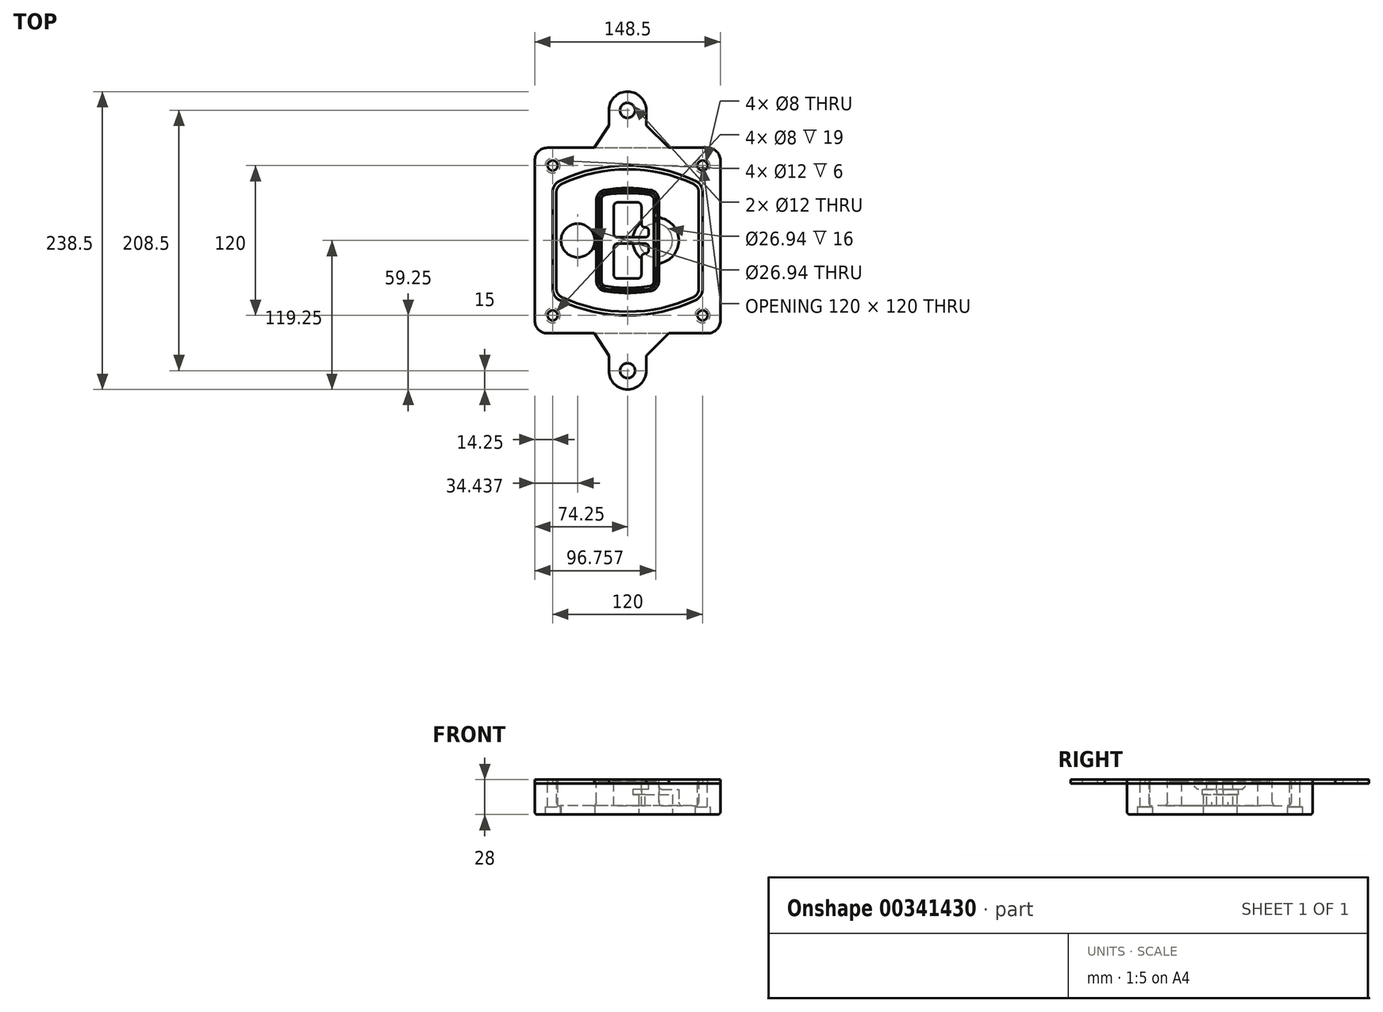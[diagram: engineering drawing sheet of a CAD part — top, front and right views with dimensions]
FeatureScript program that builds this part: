
annotation { "Feature Type Name" : "Feature", "Feature Type Description" : "" }
export const myFeature = defineFeature(function(context is Context, id is Id, definition is map)
    precondition{}
    {
        {
            var Q0;
            Q0=qCreatedBy(makeId("Top.planeOp"),FACE);
            var sketch = newSketch(context, id + "F0", { "sketchPlane" : qUnion([Q0])});
            skPoint(sketch, "E0.rect.middle", {"position": v(0, 0) * mm});
            skLineSegment(sketch, "E1.bottom", {"start": v(-64.25, -74.25) * mm, "end": v(64.25, -74.25) * mm});
            skLineSegment(sketch, "E1.top", {"start": v(-64.25, 74.25) * mm, "end": v(64.25, 74.25) * mm});
            skLineSegment(sketch, "E1.left", {"start": v(-74.25, -64.25) * mm, "end": v(-74.25, 64.25) * mm});
            skLineSegment(sketch, "E1.right", {"start": v(74.25, -64.25) * mm, "end": v(74.25, 64.25) * mm});
            skLineSegment(sketch, "E2", {"start": v(-74.25, 74.25) * mm, "end": v(74.25, -74.25) * mm, "construction": true});
            skLineSegment(sketch, "E3", {"start": v(74.25, 74.25) * mm, "end": v(-74.25, -74.25) * mm, "construction": true});
            skCircle(sketch, "E4", {"center": v(-60, 60) * mm, "radius": 4 * mm});
            skCircle(sketch, "E5", {"center": v(60, 60) * mm, "radius": 4 * mm});
            skCircle(sketch, "E6", {"center": v(60, -60) * mm, "radius": 4 * mm});
            skCircle(sketch, "E7", {"center": v(-60, -60) * mm, "radius": 4 * mm});
            skLineSegment(sketch, "E8", {"start": v(-60, 60) * mm, "end": v(60, 60) * mm, "construction": true});
            skLineSegment(sketch, "E9", {"start": v(60, 60) * mm, "end": v(60, -60) * mm, "construction": true});
            skLineSegment(sketch, "E10", {"start": v(60, -60) * mm, "end": v(-60, -60) * mm, "construction": true});
            skLineSegment(sketch, "E11", {"start": v(-60, -60) * mm, "end": v(-60, 60) * mm, "construction": true});
            skLineSegment(sketch, "E12", {"start": v(-60, 38.83) * mm, "end": v(-60, -38.83) * mm});
            skLineSegment(sketch, "E13", {"start": v(60, 38.83) * mm, "end": v(60, -38.83) * mm});
            skArc(sketch, "E14", {"start": v(54.26, 47.88) * mm, "mid": v(0, 60) * mm, "end": v(-54.26, 47.88) * mm});
            skArc(sketch, "E15", {"start": v(-54.26, -47.88) * mm, "mid": v(0, -60) * mm, "end": v(54.26, -47.88) * mm});
            skLineSegment(sketch, "E16", {"start": v(-60, 0) * mm, "end": v(60, 0) * mm, "construction": true});
            skPoint(sketch, "E17.visualSharp", {"position": v(-60, -45) * mm});
            skArc(sketch, "E17.filletArc", {"start": v(-60, -38.83) * mm, "mid": v(-58.44, -44.2) * mm, "end": v(-54.26, -47.88) * mm});
            skPoint(sketch, "E18.visualSharp", {"position": v(-60, 45) * mm});
            skArc(sketch, "E18.filletArc", {"start": v(-54.26, 47.88) * mm, "mid": v(-58.44, 44.2) * mm, "end": v(-60, 38.83) * mm});
            skPoint(sketch, "E19.visualSharp", {"position": v(60, 45) * mm});
            skArc(sketch, "E19.filletArc", {"start": v(60, 38.83) * mm, "mid": v(58.44, 44.2) * mm, "end": v(54.26, 47.88) * mm});
            skPoint(sketch, "E20.visualSharp", {"position": v(60, -45) * mm});
            skArc(sketch, "E20.filletArc", {"start": v(54.26, -47.88) * mm, "mid": v(58.44, -44.2) * mm, "end": v(60, -38.83) * mm});
            skPoint(sketch, "E21.visualSharp", {"position": v(-74.25, 74.25) * mm});
            skArc(sketch, "E21.filletArc", {"start": v(-64.25, 74.25) * mm, "mid": v(-71.32, 71.32) * mm, "end": v(-74.25, 64.25) * mm});
            skPoint(sketch, "E22.visualSharp", {"position": v(74.25, 74.25) * mm});
            skArc(sketch, "E22.filletArc", {"start": v(74.25, 64.25) * mm, "mid": v(71.32, 71.32) * mm, "end": v(64.25, 74.25) * mm});
            skPoint(sketch, "E23.visualSharp", {"position": v(74.25, -74.25) * mm});
            skArc(sketch, "E23.filletArc", {"start": v(64.25, -74.25) * mm, "mid": v(71.32, -71.32) * mm, "end": v(74.25, -64.25) * mm});
            skPoint(sketch, "E24.visualSharp", {"position": v(-74.25, -74.25) * mm});
            skArc(sketch, "E24.filletArc", {"start": v(-74.25, -64.25) * mm, "mid": v(-71.32, -71.32) * mm, "end": v(-64.25, -74.25) * mm});
            skArc(sketch, "E25.0", {"start": v(57, 38.83) * mm, "mid": v(55.9, 42.58) * mm, "end": v(52.98, 45.17) * mm});
            skLineSegment(sketch, "E25.1", {"start": v(57, 38.83) * mm, "end": v(57, -38.83) * mm});
            skArc(sketch, "E25.2", {"start": v(52.98, -45.17) * mm, "mid": v(55.9, -42.58) * mm, "end": v(57, -38.83) * mm});
            skArc(sketch, "E25.3", {"start": v(-52.98, -45.17) * mm, "mid": v(0, -57) * mm, "end": v(52.98, -45.17) * mm});
            skArc(sketch, "E25.4", {"start": v(-57, -38.83) * mm, "mid": v(-55.9, -42.58) * mm, "end": v(-52.98, -45.17) * mm});
            skArc(sketch, "E25.5", {"start": v(52.98, 45.17) * mm, "mid": v(0, 57) * mm, "end": v(-52.98, 45.17) * mm});
            skLineSegment(sketch, "E25.6", {"start": v(-57, 38.83) * mm, "end": v(-57, -38.83) * mm});
            skArc(sketch, "E25.7", {"start": v(-52.98, 45.17) * mm, "mid": v(-55.9, 42.58) * mm, "end": v(-57, 38.83) * mm});
            skArc(sketch, "E26.0", {"start": v(-55.96, 51.5) * mm, "mid": v(-61.82, 46.33) * mm, "end": v(-64, 38.83) * mm});
            skArc(sketch, "E26.1", {"start": v(55.96, 51.5) * mm, "mid": v(0, 64) * mm, "end": v(-55.96, 51.5) * mm});
            skArc(sketch, "E26.2", {"start": v(64, 38.83) * mm, "mid": v(61.82, 46.33) * mm, "end": v(55.96, 51.5) * mm});
            skLineSegment(sketch, "E26.3", {"start": v(64, 38.83) * mm, "end": v(64, -38.83) * mm});
            skArc(sketch, "E26.4", {"start": v(55.96, -51.5) * mm, "mid": v(61.82, -46.33) * mm, "end": v(64, -38.83) * mm});
            skLineSegment(sketch, "E26.5", {"start": v(-64, 38.83) * mm, "end": v(-64, -38.83) * mm});
            skArc(sketch, "E26.6", {"start": v(-55.96, -51.5) * mm, "mid": v(0, -64) * mm, "end": v(55.96, -51.5) * mm});
            skArc(sketch, "E26.7", {"start": v(-64, -38.83) * mm, "mid": v(-61.82, -46.33) * mm, "end": v(-55.96, -51.5) * mm});
            skSolve(sketch);
        }
        {
            var Q0;
            Q0=makeQuery(id+"F0.imprint","IMPRINT",FACE,{"disambiguationData":[TD([[makeQuery(id+"F0.imprint","IMPRINT",EDGE,{"derivedFrom":sQuery(id+"F0.wireOp",EDGE,"E1.bottom")}),1.0]])]});
            var Q1;
            Q1=makeQuery(id+"F0.imprint","IMPRINT",FACE,{"disambiguationData":[TD([[makeQuery(id+"F0.imprint","IMPRINT",EDGE,{"derivedFrom":sQuery(id+"F0.wireOp",EDGE,"E12")}),1.0]])]});
            var Q2;
            Q2=makeQuery(id+"F0.imprint","IMPRINT",FACE,{"disambiguationData":[TD([[makeQuery(id+"F0.imprint","IMPRINT",EDGE,{"derivedFrom":sQuery(id+"F0.wireOp",EDGE,"E25.0")}),1.0]])]});
            var Q3;
            Q3=makeQuery(id+"F0.imprint","IMPRINT",FACE,{"disambiguationData":[TD([[makeQuery(id+"F0.imprint","IMPRINT",EDGE,{"derivedFrom":sQuery(id+"F0.wireOp",EDGE,"E12")}),-1.0]])]});
            extrude(context, id + "F1", {"entities" : qUnion([Q0, Q1, Q2, Q3]), "oppositeDirection" : true, "depth" : 25 * mm});
        }
        {
            var Q0;
            Q0=makeQuery(id+"F0.imprint","IMPRINT",FACE,{"disambiguationData":[TD([[makeQuery(id+"F0.imprint","IMPRINT",EDGE,{"derivedFrom":sQuery(id+"F0.wireOp",EDGE,"E12")}),1.0]])]});
            extrude(context, id + "F2", {"entities" : qUnion([Q0]), "operationType" : NewBodyOperationType.ADD, "depth" : 3 * mm});
        }
        {
            var Q0;
            Q0=makeQuery(id+"F0.imprint","IMPRINT",FACE,{"disambiguationData":[TD([[makeQuery(id+"F0.imprint","IMPRINT",EDGE,{"derivedFrom":sQuery(id+"F0.wireOp",EDGE,"E25.0")}),1.0]])]});
            extrude(context, id + "F3", {"entities" : qUnion([Q0]), "operationType" : NewBodyOperationType.REMOVE, "oppositeDirection" : true, "depth" : 18 * mm});
        }
        {
            var Q0;
            Q0=makeQuery(id+"F2.opExtrude","CAP_FACE",FACE,{"disambiguationData":[OSD([sQuery(id+"F0.wireOp",EDGE,"E12"),sQuery(id+"F0.wireOp",EDGE,"E13"),sQuery(id+"F0.wireOp",EDGE,"E14"),sQuery(id+"F0.wireOp",EDGE,"E15"),sQuery(id+"F0.wireOp",EDGE,"E17.filletArc"),sQuery(id+"F0.wireOp",EDGE,"E18.filletArc"),sQuery(id+"F0.wireOp",EDGE,"E19.filletArc"),sQuery(id+"F0.wireOp",EDGE,"E20.filletArc"),sQuery(id+"F0.wireOp",EDGE,"E25.0"),sQuery(id+"F0.wireOp",EDGE,"E25.1"),sQuery(id+"F0.wireOp",EDGE,"E25.2"),sQuery(id+"F0.wireOp",EDGE,"E25.3"),sQuery(id+"F0.wireOp",EDGE,"E25.4"),sQuery(id+"F0.wireOp",EDGE,"E25.5"),sQuery(id+"F0.wireOp",EDGE,"E25.6"),sQuery(id+"F0.wireOp",EDGE,"E25.7")])],"isStart":false});
            var sketch = newSketch(context, id + "F4", { "sketchPlane" : qUnion([Q0])});
            skArc(sketch, "E27.0", {"start": v(-18.34, -40.45) * mm, "mid": v(0, -42) * mm, "end": v(18.34, -40.45) * mm});
            skArc(sketch, "E28.0", {"start": v(18.34, 40.45) * mm, "mid": v(0, 42) * mm, "end": v(-18.34, 40.45) * mm});
            skLineSegment(sketch, "E29", {"start": v(-25, 32.57) * mm, "end": v(-25, -32.57) * mm});
            skLineSegment(sketch, "E30", {"start": v(25, 32.57) * mm, "end": v(25, -32.57) * mm});
            skLineSegment(sketch, "E31", {"start": v(-25, 39.1) * mm, "end": v(25, 39.1) * mm, "construction": true});
            skLineSegment(sketch, "E32", {"start": v(-25, -39.1) * mm, "end": v(25, -39.1) * mm, "construction": true});
            skPoint(sketch, "E33.visualSharp", {"position": v(-25, 39.1) * mm});
            skArc(sketch, "E33.filletArc", {"start": v(-18.34, 40.45) * mm, "mid": v(-23.11, 37.73) * mm, "end": v(-25, 32.57) * mm});
            skPoint(sketch, "E34.visualSharp", {"position": v(25, 39.1) * mm});
            skArc(sketch, "E34.filletArc", {"start": v(25, 32.57) * mm, "mid": v(23.11, 37.73) * mm, "end": v(18.34, 40.45) * mm});
            skPoint(sketch, "E35.visualSharp", {"position": v(25, -39.1) * mm});
            skArc(sketch, "E35.filletArc", {"start": v(18.34, -40.45) * mm, "mid": v(23.11, -37.73) * mm, "end": v(25, -32.57) * mm});
            skPoint(sketch, "E36.visualSharp", {"position": v(-25, -39.1) * mm});
            skArc(sketch, "E36.filletArc", {"start": v(-25, -32.57) * mm, "mid": v(-23.11, -37.73) * mm, "end": v(-18.34, -40.45) * mm});
            skArc(sketch, "E37.0", {"start": v(52.98, 45.17) * mm, "mid": v(0, 57) * mm, "end": v(-52.98, 45.17) * mm});
            skArc(sketch, "E37.1", {"start": v(-52.98, 45.17) * mm, "mid": v(-55.9, 42.58) * mm, "end": v(-57, 38.83) * mm});
            skLineSegment(sketch, "E37.2", {"start": v(-57, 38.83) * mm, "end": v(-57, -38.83) * mm});
            skArc(sketch, "E37.3", {"start": v(-57, -38.83) * mm, "mid": v(-55.9, -42.58) * mm, "end": v(-52.98, -45.17) * mm});
            skArc(sketch, "E37.4", {"start": v(-52.98, -45.17) * mm, "mid": v(0, -57) * mm, "end": v(52.98, -45.17) * mm});
            skArc(sketch, "E37.5", {"start": v(52.98, -45.17) * mm, "mid": v(55.9, -42.58) * mm, "end": v(57, -38.83) * mm});
            skLineSegment(sketch, "E37.6", {"start": v(57, 38.83) * mm, "end": v(57, -38.83) * mm});
            skArc(sketch, "E37.7", {"start": v(57, 38.83) * mm, "mid": v(55.9, 42.58) * mm, "end": v(52.98, 45.17) * mm});
            skLineSegment(sketch, "E38.0", {"start": v(23, 32.57) * mm, "end": v(23, -32.57) * mm});
            skArc(sketch, "E38.1", {"start": v(18, -38.48) * mm, "mid": v(21.58, -36.44) * mm, "end": v(23, -32.57) * mm});
            skArc(sketch, "E38.2", {"start": v(-18, -38.48) * mm, "mid": v(0, -40) * mm, "end": v(18, -38.48) * mm});
            skArc(sketch, "E38.3", {"start": v(-23, -32.57) * mm, "mid": v(-21.58, -36.44) * mm, "end": v(-18, -38.48) * mm});
            skLineSegment(sketch, "E38.4", {"start": v(-23, 32.57) * mm, "end": v(-23, -32.57) * mm});
            skArc(sketch, "E38.5", {"start": v(23, 32.57) * mm, "mid": v(21.58, 36.44) * mm, "end": v(18, 38.48) * mm});
            skArc(sketch, "E38.6", {"start": v(-18, 38.48) * mm, "mid": v(-21.58, 36.44) * mm, "end": v(-23, 32.57) * mm});
            skArc(sketch, "E38.7", {"start": v(18, 38.48) * mm, "mid": v(0, 40) * mm, "end": v(-18, 38.48) * mm});
            skArc(sketch, "E39.0", {"start": v(21, 32.57) * mm, "mid": v(20.06, 35.15) * mm, "end": v(17.67, 36.5) * mm});
            skLineSegment(sketch, "E39.1", {"start": v(21, 32.57) * mm, "end": v(21, -32.57) * mm});
            skArc(sketch, "E39.2", {"start": v(17.67, -36.5) * mm, "mid": v(20.06, -35.15) * mm, "end": v(21, -32.57) * mm});
            skArc(sketch, "E39.3", {"start": v(-17.67, -36.5) * mm, "mid": v(0, -38) * mm, "end": v(17.67, -36.5) * mm});
            skArc(sketch, "E39.4", {"start": v(-21, -32.57) * mm, "mid": v(-20.06, -35.15) * mm, "end": v(-17.67, -36.5) * mm});
            skArc(sketch, "E39.5", {"start": v(17.67, 36.5) * mm, "mid": v(0, 38) * mm, "end": v(-17.67, 36.5) * mm});
            skLineSegment(sketch, "E39.6", {"start": v(-21, 32.57) * mm, "end": v(-21, -32.57) * mm});
            skArc(sketch, "E39.7", {"start": v(-17.67, 36.5) * mm, "mid": v(-20.06, 35.15) * mm, "end": v(-21, 32.57) * mm});
            skLineSegment(sketch, "E40", {"start": v(-25, 0) * mm, "end": v(25, 0) * mm, "construction": true});
            skLineSegment(sketch, "E41", {"start": v(-11, 5.5) * mm, "end": v(-11, 27.5) * mm});
            skLineSegment(sketch, "E42", {"start": v(-8, 30.5) * mm, "end": v(8, 30.5) * mm});
            skLineSegment(sketch, "E43", {"start": v(11, 27.5) * mm, "end": v(11, 13.5) * mm});
            skLineSegment(sketch, "E44", {"start": v(14, 10.5) * mm, "end": v(14, 10.5) * mm});
            skLineSegment(sketch, "E45", {"start": v(17, 7.5) * mm, "end": v(17, 5.5) * mm});
            skLineSegment(sketch, "E46", {"start": v(14, 2.5) * mm, "end": v(-8, 2.5) * mm});
            skPoint(sketch, "E47.visualSharp", {"position": v(-11, 30.5) * mm});
            skArc(sketch, "E47.filletArc", {"start": v(-8, 30.5) * mm, "mid": v(-10.12, 29.62) * mm, "end": v(-11, 27.5) * mm});
            skPoint(sketch, "E48.visualSharp", {"position": v(11, 30.5) * mm});
            skArc(sketch, "E48.filletArc", {"start": v(11, 27.5) * mm, "mid": v(10.12, 29.62) * mm, "end": v(8, 30.5) * mm});
            skPoint(sketch, "E49.visualSharp", {"position": v(11, 10.5) * mm});
            skArc(sketch, "E49.filletArc", {"start": v(11, 13.5) * mm, "mid": v(11.88, 11.38) * mm, "end": v(14, 10.5) * mm});
            skPoint(sketch, "E50.visualSharp", {"position": v(17, 10.5) * mm});
            skArc(sketch, "E50.filletArc", {"start": v(17, 7.5) * mm, "mid": v(16.12, 9.62) * mm, "end": v(14, 10.5) * mm});
            skPoint(sketch, "E51.visualSharp", {"position": v(17, 2.5) * mm});
            skArc(sketch, "E51.filletArc", {"start": v(14, 2.5) * mm, "mid": v(16.12, 3.38) * mm, "end": v(17, 5.5) * mm});
            skPoint(sketch, "E52.visualSharp", {"position": v(-11, 2.5) * mm});
            skArc(sketch, "E52.filletArc", {"start": v(-11, 5.5) * mm, "mid": v(-10.12, 3.38) * mm, "end": v(-8, 2.5) * mm});
            skLineSegment(sketch, "E53.0.MirrorCS", {"start": v(14, -2.5) * mm, "end": v(-8, -2.5) * mm});
            skArc(sketch, "E54.0.MirrorCS", {"start": v(-11, -5.5) * mm, "mid": v(-10.12, -3.38) * mm, "end": v(-8, -2.5) * mm});
            skLineSegment(sketch, "E55.0.MirrorCS", {"start": v(-11, -5.5) * mm, "end": v(-11, -27.5) * mm});
            skArc(sketch, "E56.0.MirrorCS", {"start": v(-8, -30.5) * mm, "mid": v(-10.12, -29.62) * mm, "end": v(-11, -27.5) * mm});
            skLineSegment(sketch, "E57.0.MirrorCS", {"start": v(-8, -30.5) * mm, "end": v(8, -30.5) * mm});
            skArc(sketch, "E58.0.MirrorCS", {"start": v(11, -27.5) * mm, "mid": v(10.12, -29.62) * mm, "end": v(8, -30.5) * mm});
            skLineSegment(sketch, "E59.0.MirrorCS", {"start": v(11, -27.5) * mm, "end": v(11, -13.5) * mm});
            skArc(sketch, "E60.0.MirrorCS", {"start": v(11, -13.5) * mm, "mid": v(11.88, -11.38) * mm, "end": v(14, -10.5) * mm});
            skArc(sketch, "E61.0.MirrorCS", {"start": v(17, -7.5) * mm, "mid": v(16.12, -9.62) * mm, "end": v(14, -10.5) * mm});
            skLineSegment(sketch, "E62.0.MirrorCS", {"start": v(17, -7.5) * mm, "end": v(17, -5.5) * mm});
            skArc(sketch, "E63.0.MirrorCS", {"start": v(14, -2.5) * mm, "mid": v(16.12, -3.38) * mm, "end": v(17, -5.5) * mm});
            skSolve(sketch);
        }
        {
            var Q0;
            Q0=makeQuery(id+"F4.imprint","IMPRINT",FACE,{"disambiguationData":[TD([[makeQuery(id+"F4.imprint","IMPRINT",EDGE,{"derivedFrom":sQuery(id+"F4.wireOp",EDGE,"E27.0")}),1.0]])]});
            var Q1;
            Q1=makeQuery(id+"F4.imprint","IMPRINT",FACE,{"disambiguationData":[TD([[makeQuery(id+"F4.imprint","IMPRINT",EDGE,{"derivedFrom":sQuery(id+"F4.wireOp",EDGE,"E38.0")}),-1.0]])]});
            var Q2;
            Q2=makeQuery(id+"F4.imprint","IMPRINT",FACE,{"disambiguationData":[TD([[makeQuery(id+"F4.imprint","IMPRINT",EDGE,{"derivedFrom":sQuery(id+"F4.wireOp",EDGE,"E39.0")}),1.0]])]});
            extrude(context, id + "F5", {"entities" : qUnion([Q0, Q1, Q2]), "operationType" : NewBodyOperationType.ADD, "endBound" : BoundingType.UP_TO_NEXT, "oppositeDirection" : true, "depth" : 25 * mm});
        }
        {
            var Q0;
            Q0=makeQuery(id+"F4.imprint","IMPRINT",FACE,{"disambiguationData":[TD([[makeQuery(id+"F4.imprint","IMPRINT",EDGE,{"derivedFrom":sQuery(id+"F4.wireOp",EDGE,"E38.0")}),-1.0]])]});
            extrude(context, id + "F6", {"entities" : qUnion([Q0]), "operationType" : NewBodyOperationType.REMOVE, "oppositeDirection" : true, "depth" : 2 * mm});
        }
        {
            var Q0;
            Q0=makeQuery(id+"F1.opExtrude","CAP_FACE",FACE,{"disambiguationData":[OSD([sQuery(id+"F0.wireOp",EDGE,"E1.bottom"),sQuery(id+"F0.wireOp",EDGE,"E1.top"),sQuery(id+"F0.wireOp",EDGE,"E1.left"),sQuery(id+"F0.wireOp",EDGE,"E1.right"),sQuery(id+"F0.wireOp",EDGE,"E4"),sQuery(id+"F0.wireOp",EDGE,"E5"),sQuery(id+"F0.wireOp",EDGE,"E6"),sQuery(id+"F0.wireOp",EDGE,"E7"),sQuery(id+"F0.wireOp",EDGE,"E21.filletArc"),sQuery(id+"F0.wireOp",EDGE,"E22.filletArc"),sQuery(id+"F0.wireOp",EDGE,"E23.filletArc"),sQuery(id+"F0.wireOp",EDGE,"E24.filletArc")])],"isStart":false});
            var sketch = newSketch(context, id + "F7", { "sketchPlane" : qUnion([Q0])});
            skCircle(sketch, "E64", {"center": v(22.5, 0) * mm, "radius": 13.47 * mm});
            skCircle(sketch, "E65", {"center": v(-39.81, 0) * mm, "radius": 13.47 * mm});
            skLineSegment(sketch, "E66", {"start": v(74.25, 0) * mm, "end": v(-74.25, 0) * mm});
            skCircle(sketch, "E67", {"center": v(22.5, 0) * mm, "radius": 18.47 * mm});
            skCircle(sketch, "E68", {"center": v(60, -60) * mm, "radius": 6 * mm});
            skCircle(sketch, "E69", {"center": v(-60, -60) * mm, "radius": 6 * mm});
            skCircle(sketch, "E70", {"center": v(-60, 60) * mm, "radius": 6 * mm});
            skCircle(sketch, "E71", {"center": v(60, 60) * mm, "radius": 6 * mm});
            skSolve(sketch);
        }
        {
            var Q0;
            {var subQ1=sQuery(id+"F7.wireOp",EDGE,"E66");var subQ4=sQuery(id+"F7.wireOp",EDGE,"E64");var subQ6=makeQuery(id+"F7.imprint","INTERSECT",VERTEX,{"disambiguationData":[OD(0.0)],"derivedFrom":[subQ4,subQ1]});Q0=makeQuery(id+"F7.imprint","IMPRINT",FACE,{"disambiguationData":[TD([[makeQuery(id+"F7.imprint","IMPRINT",EDGE,{"disambiguationData":[TD([[subQ6,-1.0]])],"derivedFrom":subQ4}),-1.0]])]});}
            var Q1;
            {var subQ0=sQuery(id+"F7.wireOp",EDGE,"E66");var subQ1=sQuery(id+"F7.wireOp",EDGE,"E64");var subQ3=makeQuery(id+"F7.imprint","INTERSECT",VERTEX,{"disambiguationData":[OD(0.0)],"derivedFrom":[subQ1,subQ0]});Q1=makeQuery(id+"F7.imprint","IMPRINT",FACE,{"disambiguationData":[TD([[makeQuery(id+"F7.imprint","IMPRINT",EDGE,{"disambiguationData":[TD([[subQ3,-1.0]])],"derivedFrom":subQ1}),1.0]])]});}
            var Q2;
            {var subQ0=sQuery(id+"F7.wireOp",EDGE,"E66");var subQ1=sQuery(id+"F7.wireOp",EDGE,"E64");var subQ3=makeQuery(id+"F7.imprint","INTERSECT",VERTEX,{"disambiguationData":[OD(0.0)],"derivedFrom":[subQ1,subQ0]});Q2=makeQuery(id+"F7.imprint","IMPRINT",FACE,{"disambiguationData":[TD([[makeQuery(id+"F7.imprint","IMPRINT",EDGE,{"disambiguationData":[TD([[subQ3,1.0]])],"derivedFrom":subQ1}),1.0]])]});}
            var Q3;
            {var subQ1=sQuery(id+"F7.wireOp",EDGE,"E66");var subQ4=sQuery(id+"F7.wireOp",EDGE,"E64");var subQ6=makeQuery(id+"F7.imprint","INTERSECT",VERTEX,{"disambiguationData":[OD(0.0)],"derivedFrom":[subQ4,subQ1]});Q3=makeQuery(id+"F7.imprint","IMPRINT",FACE,{"disambiguationData":[TD([[makeQuery(id+"F7.imprint","IMPRINT",EDGE,{"disambiguationData":[TD([[subQ6,1.0]])],"derivedFrom":subQ4}),-1.0]])]});}
            extrude(context, id + "F8", {"entities" : qUnion([Q0, Q1, Q2, Q3]), "operationType" : NewBodyOperationType.ADD, "oppositeDirection" : true, "depth" : 20 * mm});
        }
        {
            var Q0;
            {var subQ0=sQuery(id+"F7.wireOp",EDGE,"E66");var subQ1=sQuery(id+"F7.wireOp",EDGE,"E64");var subQ3=makeQuery(id+"F7.imprint","INTERSECT",VERTEX,{"disambiguationData":[OD(0.0)],"derivedFrom":[subQ1,subQ0]});Q0=makeQuery(id+"F7.imprint","IMPRINT",FACE,{"disambiguationData":[TD([[makeQuery(id+"F7.imprint","IMPRINT",EDGE,{"disambiguationData":[TD([[subQ3,-1.0]])],"derivedFrom":subQ1}),1.0]])]});}
            var Q1;
            {var subQ0=sQuery(id+"F7.wireOp",EDGE,"E66");var subQ1=sQuery(id+"F7.wireOp",EDGE,"E64");var subQ3=makeQuery(id+"F7.imprint","INTERSECT",VERTEX,{"disambiguationData":[OD(0.0)],"derivedFrom":[subQ1,subQ0]});Q1=makeQuery(id+"F7.imprint","IMPRINT",FACE,{"disambiguationData":[TD([[makeQuery(id+"F7.imprint","IMPRINT",EDGE,{"disambiguationData":[TD([[subQ3,1.0]])],"derivedFrom":subQ1}),1.0]])]});}
            extrude(context, id + "F9", {"entities" : qUnion([Q0, Q1]), "operationType" : NewBodyOperationType.REMOVE, "oppositeDirection" : true, "depth" : 16 * mm});
        }
        {
            var Q0;
            {var subQ0=sQuery(id+"F7.wireOp",EDGE,"E66");var subQ1=sQuery(id+"F7.wireOp",EDGE,"E65");var subQ3=makeQuery(id+"F7.imprint","INTERSECT",VERTEX,{"disambiguationData":[OD(0.0)],"derivedFrom":[subQ1,subQ0]});Q0=makeQuery(id+"F7.imprint","IMPRINT",FACE,{"disambiguationData":[TD([[makeQuery(id+"F7.imprint","IMPRINT",EDGE,{"disambiguationData":[TD([[subQ3,-1.0]])],"derivedFrom":subQ1}),1.0]])]});}
            var Q1;
            {var subQ0=sQuery(id+"F7.wireOp",EDGE,"E66");var subQ1=sQuery(id+"F7.wireOp",EDGE,"E65");var subQ3=makeQuery(id+"F7.imprint","INTERSECT",VERTEX,{"disambiguationData":[OD(0.0)],"derivedFrom":[subQ1,subQ0]});Q1=makeQuery(id+"F7.imprint","IMPRINT",FACE,{"disambiguationData":[TD([[makeQuery(id+"F7.imprint","IMPRINT",EDGE,{"disambiguationData":[TD([[subQ3,1.0]])],"derivedFrom":subQ1}),1.0]])]});}
            extrude(context, id + "F10", {"entities" : qUnion([Q0, Q1]), "operationType" : NewBodyOperationType.REMOVE, "oppositeDirection" : true, "depth" : 25 * mm});
        }
        {
            var Q0;
            Q0=makeQuery(id+"F7.imprint","IMPRINT",FACE,{"disambiguationData":[TD([[makeQuery(id+"F7.imprint","IMPRINT",EDGE,{"derivedFrom":sQuery(id+"F7.wireOp",EDGE,"E68")}),1.0]])]});
            var Q1;
            Q1=makeQuery(id+"F7.imprint","IMPRINT",FACE,{"disambiguationData":[TD([[makeQuery(id+"F7.imprint","IMPRINT",EDGE,{"derivedFrom":makeQuery(id+"F1.opExtrude","CAP_EDGE",EDGE,{"disambiguationData":[OSD([sQuery(id+"F0.wireOp",EDGE,"E5")])],"isStart":false})}),-1.0]])]});
            var Q2;
            Q2=makeQuery(id+"F7.imprint","IMPRINT",FACE,{"disambiguationData":[TD([[makeQuery(id+"F7.imprint","IMPRINT",EDGE,{"derivedFrom":sQuery(id+"F7.wireOp",EDGE,"E69")}),1.0]])]});
            var Q3;
            Q3=makeQuery(id+"F7.imprint","IMPRINT",FACE,{"disambiguationData":[TD([[makeQuery(id+"F7.imprint","IMPRINT",EDGE,{"derivedFrom":makeQuery(id+"F1.opExtrude","CAP_EDGE",EDGE,{"disambiguationData":[OSD([sQuery(id+"F0.wireOp",EDGE,"E4")])],"isStart":false})}),-1.0]])]});
            var Q4;
            Q4=makeQuery(id+"F7.imprint","IMPRINT",FACE,{"disambiguationData":[TD([[makeQuery(id+"F7.imprint","IMPRINT",EDGE,{"derivedFrom":sQuery(id+"F7.wireOp",EDGE,"E70")}),1.0]])]});
            var Q5;
            Q5=makeQuery(id+"F7.imprint","IMPRINT",FACE,{"disambiguationData":[TD([[makeQuery(id+"F7.imprint","IMPRINT",EDGE,{"derivedFrom":makeQuery(id+"F1.opExtrude","CAP_EDGE",EDGE,{"disambiguationData":[OSD([sQuery(id+"F0.wireOp",EDGE,"E7")])],"isStart":false})}),-1.0]])]});
            var Q6;
            Q6=makeQuery(id+"F7.imprint","IMPRINT",FACE,{"disambiguationData":[TD([[makeQuery(id+"F7.imprint","IMPRINT",EDGE,{"derivedFrom":sQuery(id+"F7.wireOp",EDGE,"E71")}),1.0]])]});
            var Q7;
            Q7=makeQuery(id+"F7.imprint","IMPRINT",FACE,{"disambiguationData":[TD([[makeQuery(id+"F7.imprint","IMPRINT",EDGE,{"derivedFrom":makeQuery(id+"F1.opExtrude","CAP_EDGE",EDGE,{"disambiguationData":[OSD([sQuery(id+"F0.wireOp",EDGE,"E6")])],"isStart":false})}),-1.0]])]});
            extrude(context, id + "F11", {"entities" : qUnion([Q0, Q1, Q2, Q3, Q4, Q5, Q6, Q7]), "operationType" : NewBodyOperationType.REMOVE, "oppositeDirection" : true, "depth" : 6 * mm});
        }
        {
            var Q0;
            Q0=makeQuery(id+"F9.boolean.opBoolean","COPY",FACE,{"derivedFrom":makeQuery(id+"F9.opExtrude","CAP_FACE",FACE,{"disambiguationData":[OSD([sQuery(id+"F7.wireOp",EDGE,"E64")])],"isStart":false})});
            var sketch = newSketch(context, id + "F12", { "sketchPlane" : qUnion([Q0])});
            skArc(sketch, "E72.0", {"start": v(11, 14.45) * mm, "mid": v(6.45, 9.13) * mm, "end": v(4.2, 2.5) * mm});
            skArc(sketch, "E72.1", {"start": v(4.2, -2.5) * mm, "mid": v(6.45, -9.13) * mm, "end": v(11, -14.45) * mm});
            skLineSegment(sketch, "E73", {"start": v(4.2, -2.5) * mm, "end": v(14, -2.5) * mm});
            skLineSegment(sketch, "E74.0", {"start": v(14, 2.5) * mm, "end": v(4.2, 2.5) * mm});
            skArc(sketch, "E74.1", {"start": v(14, 2.5) * mm, "mid": v(16.12, 3.38) * mm, "end": v(17, 5.5) * mm});
            skLineSegment(sketch, "E74.2", {"start": v(17, 7.5) * mm, "end": v(17, 5.5) * mm});
            skArc(sketch, "E74.3", {"start": v(17, 7.5) * mm, "mid": v(16.12, 9.62) * mm, "end": v(14, 10.5) * mm});
            skArc(sketch, "E74.4", {"start": v(11, 13.5) * mm, "mid": v(11.88, 11.38) * mm, "end": v(14, 10.5) * mm});
            skLineSegment(sketch, "E74.5", {"start": v(11, 14.45) * mm, "end": v(11, 13.5) * mm});
            skLineSegment(sketch, "E74.7", {"start": v(14, -2.5) * mm, "end": v(4.2, -2.5) * mm});
            skArc(sketch, "E74.8", {"start": v(14, -2.5) * mm, "mid": v(16.12, -3.38) * mm, "end": v(17, -5.5) * mm});
            skLineSegment(sketch, "E74.9", {"start": v(17, -7.5) * mm, "end": v(17, -5.5) * mm});
            skArc(sketch, "E74.10", {"start": v(17, -7.5) * mm, "mid": v(16.12, -9.62) * mm, "end": v(14, -10.5) * mm});
            skArc(sketch, "E74.11", {"start": v(11, -13.5) * mm, "mid": v(11.88, -11.38) * mm, "end": v(14, -10.5) * mm});
            skLineSegment(sketch, "E74.12", {"start": v(11, -14.45) * mm, "end": v(11, -13.5) * mm});
            skPoint(sketch, "E75.orphan", {"position": v(11, -27.5) * mm});
            skPoint(sketch, "E76.orphan", {"position": v(-8, -2.5) * mm});
            skPoint(sketch, "E77.orphan", {"position": v(-8, 2.5) * mm});
            skPoint(sketch, "E78.orphan", {"position": v(11, 27.5) * mm});
            skSolve(sketch);
        }
        {
            var Q0;
            {var subQ7=sQuery(id+"F12.wireOp",EDGE,"E72.0");var subQ14=sQuery(id+"F12.wireOp",EDGE,"E72.1");var subQ16=sQuery(id+"F12.wireOp",EDGE,"E74.1");var subQ18=sQuery(id+"F12.wireOp",EDGE,"E74.8");Q0=qUnion([makeQuery(id+"F12.imprint","IMPRINT",FACE,{"disambiguationData":[TD([[makeQuery(id+"F12.imprint","IMPRINT",EDGE,{"derivedFrom":subQ7}),1.0]])]}),makeQuery(id+"F12.imprint","IMPRINT",FACE,{"disambiguationData":[TD([[makeQuery(id+"F12.imprint","IMPRINT",EDGE,{"derivedFrom":subQ14}),1.0]])]}),makeQuery(id+"F12.imprint","IMPRINT",FACE,{"disambiguationData":[TD([[makeQuery(id+"F12.imprint","IMPRINT",EDGE,{"derivedFrom":subQ16}),1.0]])]}),makeQuery(id+"F12.imprint","IMPRINT",FACE,{"disambiguationData":[TD([[makeQuery(id+"F12.imprint","IMPRINT",EDGE,{"derivedFrom":subQ18}),-1.0]])]})]);}
            var Q1;
            Q1=makeQuery(id+"F5.boolean.opBoolean","SPLIT",FACE,{"disambiguationData":[TD([makeQuery(id+"F5.opExtrude","SWEPT_FACE",FACE,{"disambiguationData":[OSD([sQuery(id+"F4.wireOp",EDGE,"E41")])]})])],"derivedFrom":makeQuery(id+"F3.boolean.opBoolean","COPY",FACE,{"derivedFrom":makeQuery(id+"F3.opExtrude","CAP_FACE",FACE,{"disambiguationData":[OSD([sQuery(id+"F0.wireOp",EDGE,"E25.0"),sQuery(id+"F0.wireOp",EDGE,"E25.1"),sQuery(id+"F0.wireOp",EDGE,"E25.2"),sQuery(id+"F0.wireOp",EDGE,"E25.3"),sQuery(id+"F0.wireOp",EDGE,"E25.4"),sQuery(id+"F0.wireOp",EDGE,"E25.5"),sQuery(id+"F0.wireOp",EDGE,"E25.6"),sQuery(id+"F0.wireOp",EDGE,"E25.7")])],"isStart":false})})});
            extrude(context, id + "F13", {"entities" : qUnion([Q0]), "operationType" : NewBodyOperationType.REMOVE, "endBound" : BoundingType.UP_TO_SURFACE, "endBoundEntityFace" : qUnion([Q1]), "depth" : 25 * mm});
        }
        {
            var Q0;
            Q0=makeQuery(id+"F3.boolean.opBoolean","COPY",EDGE,{"derivedFrom":makeQuery(id+"F3.opExtrude","CAP_EDGE",EDGE,{"disambiguationData":[OSD([sQuery(id+"F0.wireOp",EDGE,"E25.6")])],"isStart":false})});
            var Q1;
            Q1=makeQuery(id+"F8.boolean.opBoolean","INTERSECT",EDGE,{"derivedFrom":[makeQuery(id+"F5.opExtrude","SWEPT_FACE",FACE,{"disambiguationData":[OSD([sQuery(id+"F4.wireOp",EDGE,"E30")])]}),makeQuery(id+"F8.opExtrude","CAP_FACE",FACE,{"disambiguationData":[OSD([sQuery(id+"F7.wireOp",EDGE,"E67")])],"isStart":false})]});
            var Q2;
            Q2=makeQuery(id+"F8.boolean.opBoolean","INTERSECT",EDGE,{"disambiguationData":[OD(1.0)],"derivedFrom":[makeQuery(id+"F5.opExtrude","SWEPT_FACE",FACE,{"disambiguationData":[OSD([sQuery(id+"F4.wireOp",EDGE,"E30")])]}),makeQuery(id+"F8.opExtrude","SWEPT_FACE",FACE,{"disambiguationData":[OSD([sQuery(id+"F7.wireOp",EDGE,"E67")])]})]});
            var Q3;
            {var subQ0=sQuery(id+"F4.wireOp",EDGE,"E30");Q3=makeQuery(id+"F8.boolean.opBoolean","SPLIT",EDGE,{"disambiguationData":[TD([makeQuery(id+"F5.opExtrude","SWEPT_FACE",FACE,{"disambiguationData":[OSD([sQuery(id+"F4.wireOp",EDGE,"E35.filletArc")])]})])],"derivedFrom":makeQuery(id+"F5.opExtrude","CAP_EDGE",EDGE,{"disambiguationData":[OSD([subQ0])],"isStart":false})});}
            var Q4;
            {var subQ0=sQuery(id+"F0.wireOp",EDGE,"E25.7");var subQ1=sQuery(id+"F0.wireOp",EDGE,"E25.1");var subQ2=sQuery(id+"F0.wireOp",EDGE,"E25.6");var subQ3=sQuery(id+"F0.wireOp",EDGE,"E25.5");var subQ4=sQuery(id+"F0.wireOp",EDGE,"E25.4");var subQ5=sQuery(id+"F0.wireOp",EDGE,"E25.0");var subQ6=sQuery(id+"F0.wireOp",EDGE,"E25.2");var subQ7=sQuery(id+"F0.wireOp",EDGE,"E25.3");Q4=makeQuery(id+"F8.boolean.opBoolean","INTERSECT",EDGE,{"derivedFrom":[makeQuery(id+"F5.boolean.opBoolean","SPLIT",FACE,{"disambiguationData":[TD([makeQuery(id+"F2.opExtrude","SWEPT_FACE",FACE,{"disambiguationData":[OSD([subQ5])]})])],"derivedFrom":makeQuery(id+"F3.boolean.opBoolean","COPY",FACE,{"derivedFrom":makeQuery(id+"F3.opExtrude","CAP_FACE",FACE,{"disambiguationData":[OSD([subQ5,subQ1,subQ6,subQ7,subQ4,subQ3,subQ2,subQ0])],"isStart":false})})}),makeQuery(id+"F8.opExtrude","SWEPT_FACE",FACE,{"disambiguationData":[OSD([sQuery(id+"F7.wireOp",EDGE,"E67")])]})]});}
            var Q5;
            Q5=makeQuery(id+"F8.boolean.opBoolean","INTERSECT",EDGE,{"disambiguationData":[OD(0.0)],"derivedFrom":[makeQuery(id+"F5.opExtrude","SWEPT_FACE",FACE,{"disambiguationData":[OSD([sQuery(id+"F4.wireOp",EDGE,"E30")])]}),makeQuery(id+"F8.opExtrude","SWEPT_FACE",FACE,{"disambiguationData":[OSD([sQuery(id+"F7.wireOp",EDGE,"E67")])]})]});
            fillet(context, id + "F14", {"entities" : qUnion([Q0, Q1, Q2, Q3, Q4, Q5]), "radius" : 3 * mm, "tangentPropagation" : true, "allowEdgeOverflow" : false});
        }
        {
            var Q0;
            Q0=makeQuery(id+"F1.opExtrude","CAP_EDGE",EDGE,{"disambiguationData":[OSD([sQuery(id+"F0.wireOp",EDGE,"E1.bottom")])],"isStart":false});
            fillet(context, id + "F15", {"entities" : qUnion([Q0]), "radius" : 2 * mm, "tangentPropagation" : true, "allowEdgeOverflow" : false});
        }
        {
            var Q0;
            {var subQ0=sQuery(id+"F0.wireOp",EDGE,"E21.filletArc");var subQ1=sQuery(id+"F0.wireOp",EDGE,"E7");var subQ2=sQuery(id+"F0.wireOp",EDGE,"E6");var subQ3=sQuery(id+"F0.wireOp",EDGE,"E5");var subQ4=sQuery(id+"F0.wireOp",EDGE,"E4");var subQ5=sQuery(id+"F0.wireOp",EDGE,"E22.filletArc");var subQ6=sQuery(id+"F0.wireOp",EDGE,"E1.bottom");var subQ7=sQuery(id+"F0.wireOp",EDGE,"E1.right");var subQ8=sQuery(id+"F0.wireOp",EDGE,"E1.top");var subQ9=sQuery(id+"F0.wireOp",EDGE,"E1.left");var subQ10=sQuery(id+"F0.wireOp",EDGE,"E23.filletArc");var subQ11=sQuery(id+"F0.wireOp",EDGE,"E24.filletArc");Q0=makeQuery(id+"F2.boolean.opBoolean","SPLIT",FACE,{"disambiguationData":[TD([makeQuery(id+"F1.opExtrude","SWEPT_FACE",FACE,{"disambiguationData":[OSD([subQ6])]})])],"derivedFrom":makeQuery(id+"F1.opExtrude","CAP_FACE",FACE,{"disambiguationData":[OSD([subQ6,subQ8,subQ9,subQ7,subQ4,subQ3,subQ2,subQ1,subQ0,subQ5,subQ10,subQ11])],"isStart":true})});}
            var sketch = newSketch(context, id + "F16", { "sketchPlane" : qUnion([Q0])});
            skLineSegment(sketch, "E79", {"start": v(0, 74.25) * mm, "end": v(0, 104.25) * mm, "construction": true});
            skCircle(sketch, "E80", {"center": v(0, 104.25) * mm, "radius": 6 * mm});
            skLineSegment(sketch, "E81", {"start": v(-15, 104.25) * mm, "end": v(-15, 92.25) * mm});
            skLineSegment(sketch, "E82", {"start": v(-15, 92.25) * mm, "end": v(-26.75, 74.25) * mm});
            skLineSegment(sketch, "E83", {"start": v(15, 104.25) * mm, "end": v(15, 92.25) * mm});
            skLineSegment(sketch, "E84", {"start": v(15, 92.25) * mm, "end": v(33, 74.25) * mm});
            skArc(sketch, "E85", {"start": v(15, 104.25) * mm, "mid": v(0, 119.25) * mm, "end": v(-15, 104.25) * mm});
            skLineSegment(sketch, "E86", {"start": v(-74.25, 0) * mm, "end": v(74.25, 0) * mm, "construction": true});
            skLineSegment(sketch, "E87.MirrorCS", {"start": v(15, -104.25) * mm, "end": v(15, -92.25) * mm});
            skLineSegment(sketch, "E88.MirrorCS", {"start": v(15, -92.25) * mm, "end": v(33, -74.25) * mm});
            skArc(sketch, "E89.MirrorCS", {"start": v(15, -104.25) * mm, "mid": v(0, -119.25) * mm, "end": v(-15, -104.25) * mm});
            skLineSegment(sketch, "E90.MirrorCS", {"start": v(-15, -104.25) * mm, "end": v(-15, -92.25) * mm});
            skCircle(sketch, "E91.MirrorC", {"center": v(0, -104.25) * mm, "radius": 6 * mm});
            skLineSegment(sketch, "E92.MirrorCS", {"start": v(0, -74.25) * mm, "end": v(0, -104.25) * mm, "construction": true});
            skLineSegment(sketch, "E93.MirrorCS", {"start": v(-15, -92.25) * mm, "end": v(-26.75, -74.25) * mm});
            skSolve(sketch);
        }
        {
            var Q0;
            Q0=makeQuery(id+"F16.imprint","IMPRINT",FACE,{"disambiguationData":[TD([[makeQuery(id+"F16.imprint","IMPRINT",EDGE,{"derivedFrom":sQuery(id+"F16.wireOp",EDGE,"E80")}),-1.0]])]});
            var Q1;
            Q1=makeQuery(id+"F16.imprint","IMPRINT",FACE,{"disambiguationData":[TD([[makeQuery(id+"F16.imprint","IMPRINT",EDGE,{"derivedFrom":makeQuery(id+"F1.opExtrude","CAP_EDGE",EDGE,{"disambiguationData":[OSD([sQuery(id+"F0.wireOp",EDGE,"E1.left")])],"isStart":true})}),-1.0]])]});
            var Q2;
            Q2=makeQuery(id+"F16.imprint","IMPRINT",FACE,{"disambiguationData":[TD([[makeQuery(id+"F16.imprint","IMPRINT",EDGE,{"derivedFrom":sQuery(id+"F16.wireOp",EDGE,"E87.MirrorCS")}),1.0]])]});
            var Q3;
            Q3=makeQuery(id+"F2.opExtrude","CAP_FACE",FACE,{"disambiguationData":[OSD([sQuery(id+"F0.wireOp",EDGE,"E12"),sQuery(id+"F0.wireOp",EDGE,"E13"),sQuery(id+"F0.wireOp",EDGE,"E14"),sQuery(id+"F0.wireOp",EDGE,"E15"),sQuery(id+"F0.wireOp",EDGE,"E17.filletArc"),sQuery(id+"F0.wireOp",EDGE,"E18.filletArc"),sQuery(id+"F0.wireOp",EDGE,"E19.filletArc"),sQuery(id+"F0.wireOp",EDGE,"E20.filletArc"),sQuery(id+"F0.wireOp",EDGE,"E25.0"),sQuery(id+"F0.wireOp",EDGE,"E25.1"),sQuery(id+"F0.wireOp",EDGE,"E25.2"),sQuery(id+"F0.wireOp",EDGE,"E25.3"),sQuery(id+"F0.wireOp",EDGE,"E25.4"),sQuery(id+"F0.wireOp",EDGE,"E25.5"),sQuery(id+"F0.wireOp",EDGE,"E25.6"),sQuery(id+"F0.wireOp",EDGE,"E25.7")])],"isStart":false});
            extrude(context, id + "F17", {"entities" : qUnion([Q0, Q1, Q2]), "endBound" : BoundingType.UP_TO_SURFACE, "endBoundEntityFace" : qUnion([Q3]), "depth" : 25 * mm});
        }
    });
